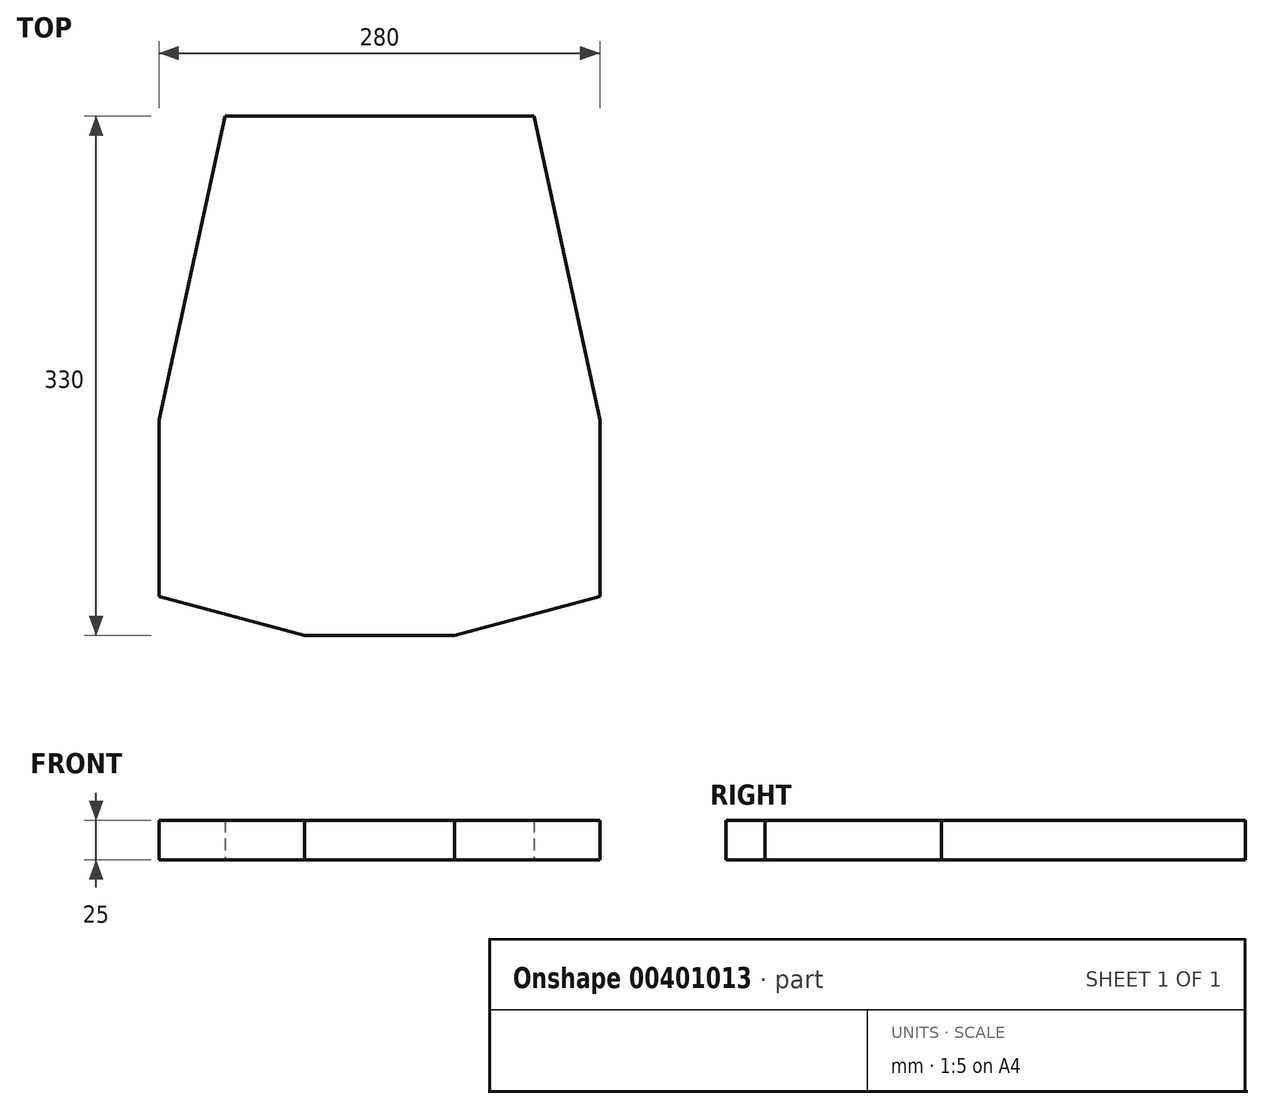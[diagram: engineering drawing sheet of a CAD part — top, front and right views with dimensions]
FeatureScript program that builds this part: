
annotation { "Feature Type Name" : "Feature", "Feature Type Description" : "" }
export const myFeature = defineFeature(function(context is Context, id is Id, definition is map)
    precondition{}
    {
        {
            var Q0;
            Q0=qCreatedBy(makeId("Top.planeOp"),FACE);
            var sketch = newSketch(context, id + "F0", { "sketchPlane" : qUnion([Q0])});
            skLineSegment(sketch, "E0", {"start": v(98.15, 164.88) * mm, "end": v(140, -28.09) * mm});
            skLineSegment(sketch, "E1", {"start": v(140, -28.09) * mm, "end": v(140, -140.34) * mm});
            skLineSegment(sketch, "E2", {"start": v(140, -140.34) * mm, "end": v(47.55, -165.12) * mm});
            skLineSegment(sketch, "E3", {"start": v(47.55, -165.12) * mm, "end": v(0, -165.12) * mm});
            skLineSegment(sketch, "E4", {"start": v(0, 164.88) * mm, "end": v(98.15, 164.88) * mm});
            skLineSegment(sketch, "E5.MirrorCS", {"start": v(0, 164.88) * mm, "end": v(-98.15, 164.88) * mm});
            skLineSegment(sketch, "E6.MirrorCS", {"start": v(-47.55, -165.12) * mm, "end": v(0, -165.12) * mm});
            skLineSegment(sketch, "E7.MirrorCS", {"start": v(-98.15, 164.88) * mm, "end": v(-140, -28.09) * mm});
            skLineSegment(sketch, "E8.MirrorCS", {"start": v(-140, -28.09) * mm, "end": v(-140, -140.34) * mm});
            skLineSegment(sketch, "E9.MirrorCS", {"start": v(-140, -140.34) * mm, "end": v(-47.55, -165.12) * mm});
            skPoint(sketch, "E10", {"position": v(-43.87, -32.27) * mm});
            skPoint(sketch, "E11", {"position": v(46.13, -32.27) * mm});
            skPoint(sketch, "E12", {"position": v(46.13, -102.27) * mm});
            skPoint(sketch, "E13", {"position": v(-43.87, -102.27) * mm});
            skPoint(sketch, "E14", {"position": v(-125.66, -71.08) * mm});
            skPoint(sketch, "E15", {"position": v(-79.97, 124.75) * mm});
            skSolve(sketch);
        }
        {
            var Q0;
            Q0=makeQuery(id+"F0.imprint","IMPRINT",FACE,{"disambiguationData":[TD([[makeQuery(id+"F0.imprint","IMPRINT",EDGE,{"derivedFrom":sQuery(id+"F0.wireOp",EDGE,"E0")}),-1.0]])]});
            extrude(context, id + "F1", {"entities" : qUnion([Q0]), "depth" : 25 * mm});
        }
    });
